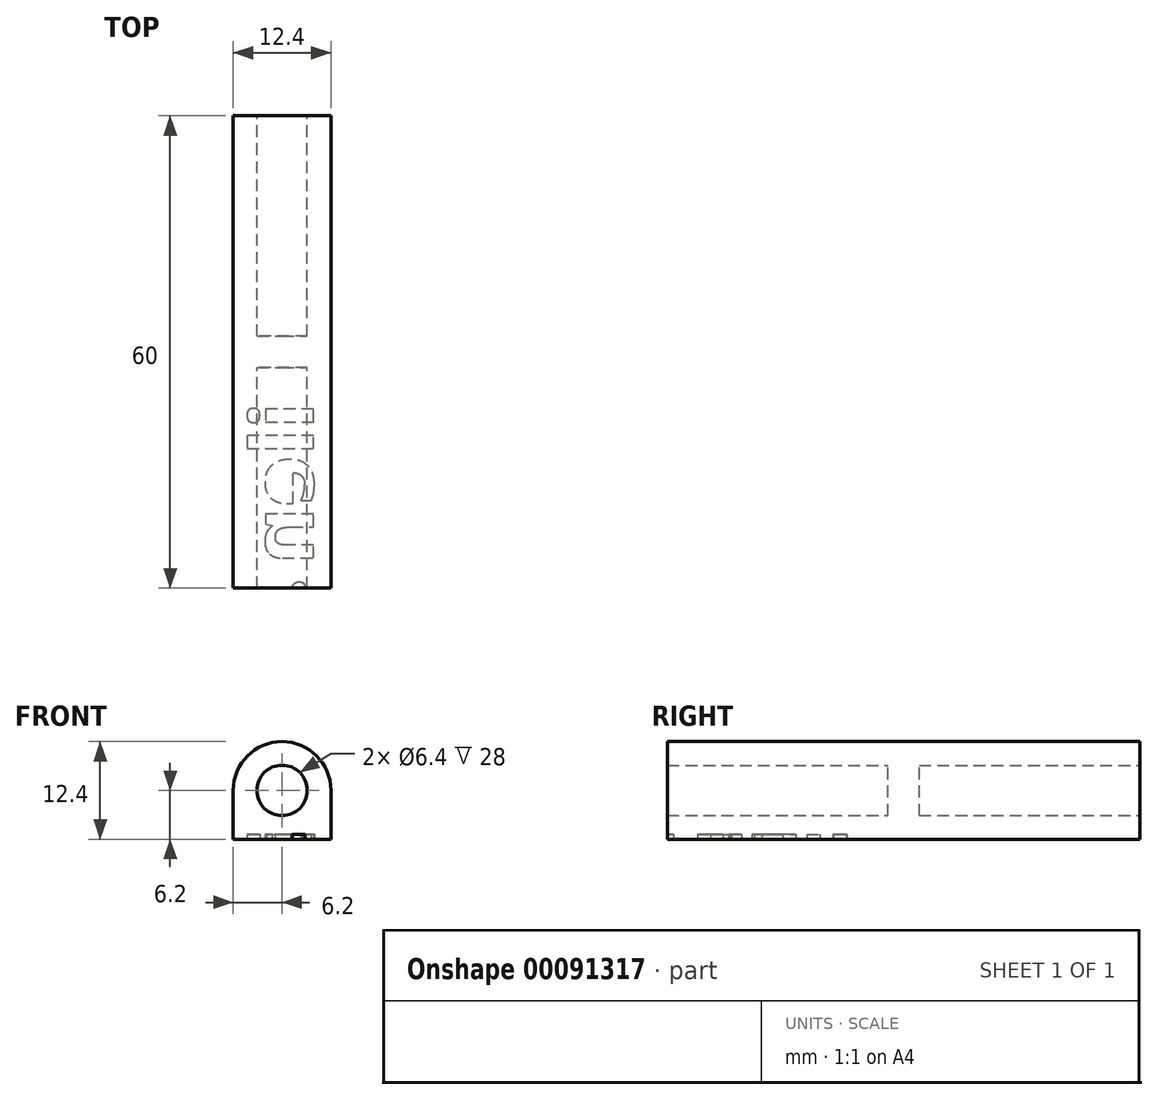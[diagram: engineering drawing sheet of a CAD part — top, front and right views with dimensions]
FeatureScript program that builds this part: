
annotation { "Feature Type Name" : "Feature", "Feature Type Description" : "" }
export const myFeature = defineFeature(function(context is Context, id is Id, definition is map)
    precondition{}
    {
        {
            var Q0;
            Q0=qCreatedBy(makeId("Front.planeOp"),FACE);
            var sketch = newSketch(context, id + "F0", { "sketchPlane" : qUnion([Q0])});
            skCircle(sketch, "E0", {"center": v(0, 0) * mm, "radius": 3.2 * mm});
            skCircle(sketch, "E1", {"center": v(0, 0) * mm, "radius": 6.2 * mm});
            skLineSegment(sketch, "E2", {"start": v(-6.2, 0) * mm, "end": v(-6.2, -6.2) * mm});
            skLineSegment(sketch, "E3", {"start": v(-6.2, -6.2) * mm, "end": v(6.2, -6.2) * mm});
            skLineSegment(sketch, "E4", {"start": v(6.2, -6.2) * mm, "end": v(6.2, 0) * mm});
            skSolve(sketch);
        }
        {
            var Q0;
            Q0=qSketchRegion(id+"F0",true);
            extrude(context, id + "F1", {"entities" : qUnion([Q0]), "endBound" : BoundingType.SYMMETRIC, "depth" : 60 * mm, "offsetDistance" : 25 * mm});
        }
        {
            var Q0;
            Q0=makeQuery(id+"F1.opExtrude","SWEPT_FACE",FACE,{"disambiguationData":[OSD([sQuery(id+"F0.wireOp",EDGE,"E3")])]});
            var sketch = newSketch(context, id + "F2", { "sketchPlane" : qUnion([Q0])});
            skText(sketch, "E5", { "text": "ilena", "fontName": "OpenSans-Bold.ttf"});
            skPoint(sketch, "E6", {"position": v(0, 13.62) * mm});
            skPoint(sketch, "E7", {"position": v(0, 30) * mm});
            skPoint(sketch, "E8", {"position": v(6.2, 0) * mm});
            const initialGuessF2  = {"E5": [0.004, 0.00638, 0, 1, 0.008]};
            skSetInitialGuess(sketch, initialGuessF2);
            skSolve(sketch);
        }
        {
            var Q0;
            Q0=makeQuery(id+"F2.imprint","IMPRINT",FACE,{"disambiguationData":[TD([[makeQuery(id+"F2.imprint","IMPRINT",EDGE,{"derivedFrom":sQuery(id+"F2.wireOp",EDGE,"E5.sketch_text.stroke-5")}),-1.0]])]});
            var Q1;
            Q1=makeQuery(id+"F2.imprint","IMPRINT",FACE,{"disambiguationData":[TD([[makeQuery(id+"F2.imprint","IMPRINT",EDGE,{"derivedFrom":sQuery(id+"F2.wireOp",EDGE,"E5.sketch_text.stroke-0")}),-1.0]])]});
            var Q2;
            Q2=makeQuery(id+"F2.imprint","IMPRINT",FACE,{"disambiguationData":[TD([[makeQuery(id+"F2.imprint","IMPRINT",EDGE,{"derivedFrom":sQuery(id+"F2.wireOp",EDGE,"E5.sketch_text.stroke-9")}),-1.0]])]});
            var Q3;
            Q3=makeQuery(id+"F2.imprint","IMPRINT",FACE,{"disambiguationData":[TD([[makeQuery(id+"F2.imprint","IMPRINT",EDGE,{"derivedFrom":sQuery(id+"F2.wireOp",EDGE,"E5.sketch_text.stroke-15")}),-1.0]])]});
            var Q4;
            Q4=makeQuery(id+"F2.imprint","IMPRINT",FACE,{"disambiguationData":[TD([[makeQuery(id+"F2.imprint","IMPRINT",EDGE,{"derivedFrom":sQuery(id+"F2.wireOp",EDGE,"E5.sketch_text.stroke-15")}),1.0]])]});
            var Q5;
            Q5=makeQuery(id+"F2.imprint","IMPRINT",FACE,{"disambiguationData":[TD([[makeQuery(id+"F2.imprint","IMPRINT",EDGE,{"derivedFrom":sQuery(id+"F2.wireOp",EDGE,"E5.sketch_text.stroke-35")}),-1.0]])]});
            var Q6;
            Q6=makeQuery(id+"F2.imprint","IMPRINT",FACE,{"disambiguationData":[TD([[makeQuery(id+"F2.imprint","IMPRINT",EDGE,{"derivedFrom":sQuery(id+"F2.wireOp",EDGE,"E5.sketch_text.stroke-70")}),1.0]])]});
            var Q7;
            Q7=makeQuery(id+"F2.imprint","IMPRINT",FACE,{"disambiguationData":[TD([[makeQuery(id+"F2.imprint","IMPRINT",EDGE,{"derivedFrom":sQuery(id+"F2.wireOp",EDGE,"E5.sketch_text.stroke-52")}),-1.0]])]});
            extrude(context, id + "F3", {"entities" : qUnion([Q0, Q1, Q2, Q3, Q4, Q5, Q6, Q7]), "operationType" : NewBodyOperationType.REMOVE, "oppositeDirection" : true, "depth" : 0.6 * mm});
        }
        {
            var Q0;
            Q0=qCreatedBy(makeId("Front.planeOp"),FACE);
            var sketch = newSketch(context, id + "F4", { "sketchPlane" : qUnion([Q0])});
            skCircle(sketch, "E9", {"center": v(0, 0) * mm, "radius": 3.2 * mm});
            skSolve(sketch);
        }
        {
            var Q0;
            Q0=makeQuery(id+"F4.imprint","IMPRINT",FACE,{"disambiguationData":[TD([[makeQuery(id+"F4.imprint","IMPRINT",EDGE,{"derivedFrom":sQuery(id+"F4.wireOp",EDGE,"E9")}),1.0]])]});
            extrude(context, id + "F5", {"entities" : qUnion([Q0]), "operationType" : NewBodyOperationType.ADD, "endBound" : BoundingType.SYMMETRIC, "depth" : 4 * mm, "offsetDistance" : 25 * mm});
        }
    });
